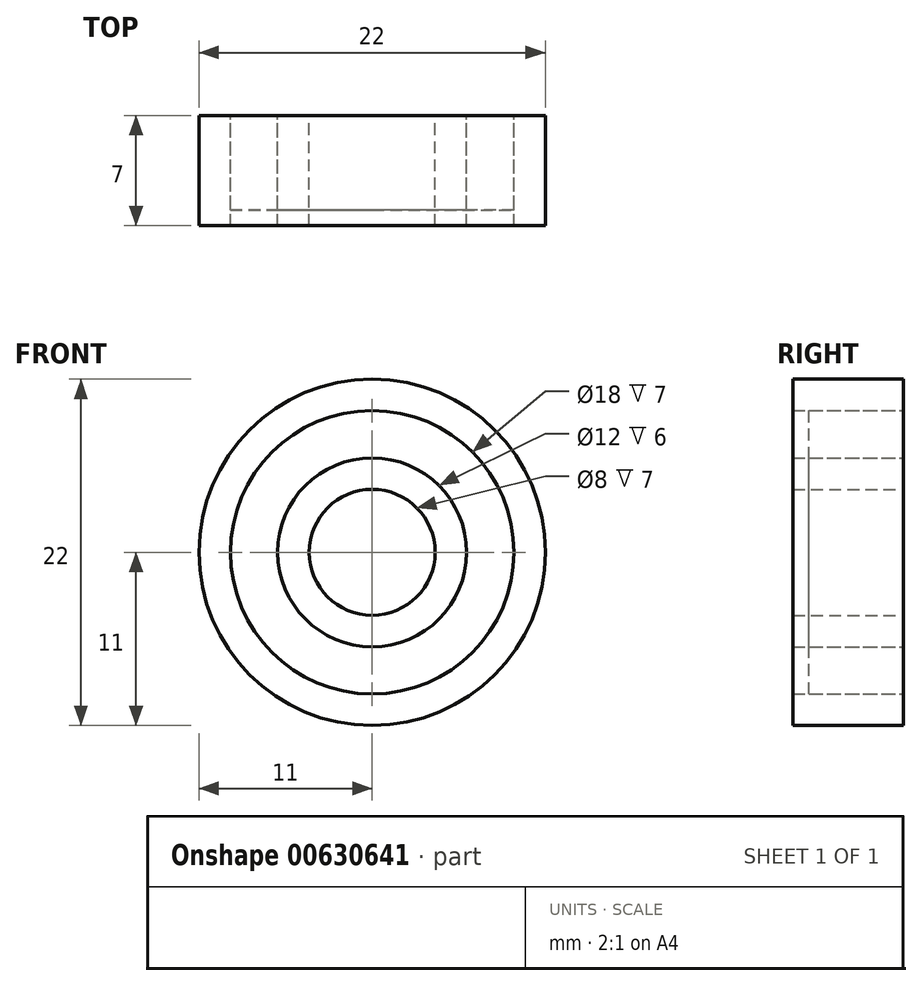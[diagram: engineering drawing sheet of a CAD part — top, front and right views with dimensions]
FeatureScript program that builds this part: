
annotation { "Feature Type Name" : "Feature", "Feature Type Description" : "" }
export const myFeature = defineFeature(function(context is Context, id is Id, definition is map)
    precondition{}
    {
        {
            var Q0;
            Q0=qCreatedBy(makeId("Front.planeOp"),FACE);
            var sketch = newSketch(context, id + "F0", { "sketchPlane" : qUnion([Q0])});
            skCircle(sketch, "E0", {"center": v(0, 0) * mm, "radius": 4 * mm});
            skCircle(sketch, "E1", {"center": v(0, 0) * mm, "radius": 11 * mm});
            skCircle(sketch, "E2", {"center": v(0, 0) * mm, "radius": 6 * mm});
            skCircle(sketch, "E3", {"center": v(0, 0) * mm, "radius": 9 * mm});
            skSolve(sketch);
        }
        {
            var Q0;
            Q0=makeQuery(id+"F0.imprint","IMPRINT",FACE,{"disambiguationData":[TD([[makeQuery(id+"F0.imprint","IMPRINT",EDGE,{"derivedFrom":sQuery(id+"F0.wireOp",EDGE,"E0")}),-1.0]])]});
            extrude(context, id + "F1", {"entities" : qUnion([Q0]), "depth" : 7 * mm, "offsetDistance" : 25 * mm});
        }
        {
            var Q0;
            Q0=makeQuery(id+"F0.imprint","IMPRINT",FACE,{"disambiguationData":[TD([[makeQuery(id+"F0.imprint","IMPRINT",EDGE,{"derivedFrom":sQuery(id+"F0.wireOp",EDGE,"E1")}),1.0]])]});
            extrude(context, id + "F2", {"entities" : qUnion([Q0]), "depth" : 7 * mm, "offsetDistance" : 25 * mm});
        }
        {
            var Q0;
            Q0=makeQuery(id+"F0.imprint","IMPRINT",FACE,{"disambiguationData":[TD([[makeQuery(id+"F0.imprint","IMPRINT",EDGE,{"derivedFrom":sQuery(id+"F0.wireOp",EDGE,"E2")}),-1.0]])]});
            extrude(context, id + "F3", {"entities" : qUnion([Q0]), "depth" : 6 * mm, "offsetDistance" : 25 * mm});
        }
    });
